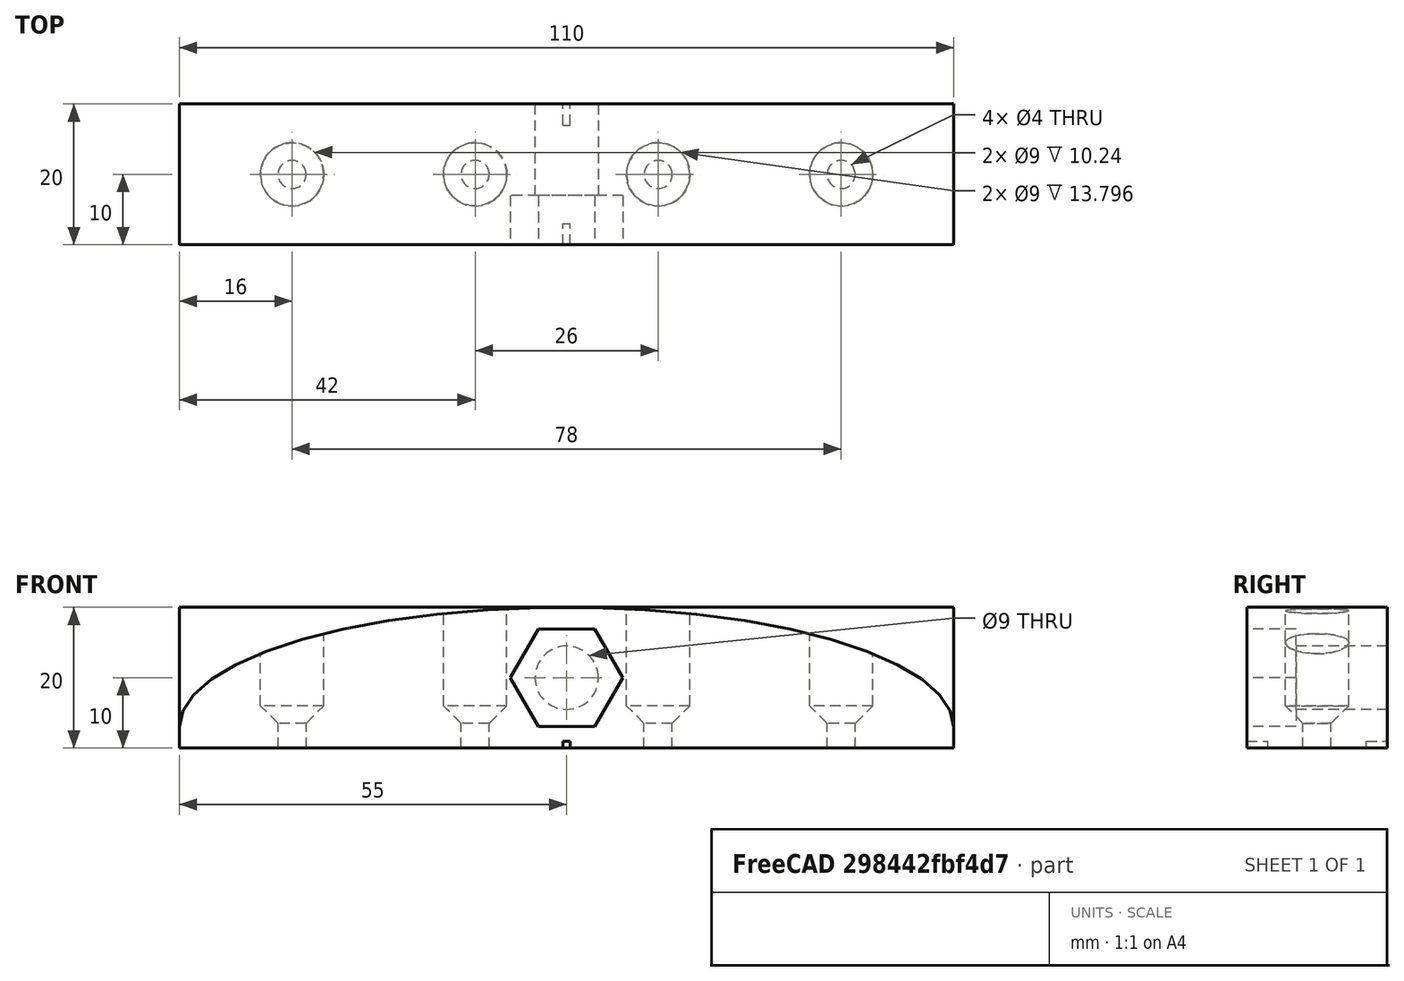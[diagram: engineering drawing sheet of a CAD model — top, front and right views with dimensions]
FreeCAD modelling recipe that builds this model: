
FCSTD DOCUMENT  (FreeCAD 0.18R4 (GitTag))
Label: Internal Support
License: All rights reserved
LicenseURL: http://en.wikipedia.org/wiki/All_rights_reserved
objects: Part::Box×5, Part::Cut×5, Part::Cylinder×4, Part::MultiFuse×4, Part::Extrusion×2, Part::Ellipse×1, Part::FeaturePython×1, Part::RegularPolygon×1, Part::Chamfer×1
note: 24 computed .brp shape members not serialized (recipe doc carries the construction recipe); baked Part::Feature solids carry a one-line shape summary decoded from their .brp

FEATURE [Part::Box] Box004  label="Signal003"
  AttacherType = Attacher::AttachEngine3D
  Height = 1
  Length = 1
  Placement = pos=(-0.5,7,0) rot=(0,0,1;0rad)
  Width = 3
FEATURE [Part::Cylinder] Cylinder005  label="Cylinder006"
  Angle = 360
  AttacherType = Attacher::AttachEngine3D
  Height = 20
  Placement = pos=(0,10,10) rot=(1,0,0;1.5708rad)
  Radius = 6.5
FEATURE [Part::Box] Box005  label="Signal004"
  AttacherType = Attacher::AttachEngine3D
  Height = 1
  Length = 1
  Placement = pos=(-0.5,-10,0) rot=(0,0,1;0rad)
  Width = 3
FEATURE [Part::Cylinder] Cylinder006  label="Hole001"
  Angle = 360
  AttacherType = Attacher::AttachEngine3D
  Height = 20
  Placement = pos=(0,10,10) rot=(1,0,0;1.5708rad)
  Radius = 4.5
FEATURE [Part::Ellipse] Ellipse
  Angle0 = 0
  Angle1 = 360
  AttacherType = Attacher::AttachEngine3D
  MajorRadius = 55
  MinorRadius = 17
  Placement = pos=(0,0,3) rot=(1,0,0;1.5708rad)
FEATURE [Part::Extrusion] Extrude002
  Base = -> Ellipse
  Dir = (0,1,0)
  DirMode = 2
  FaceMakerClass = Part::FaceMakerBullseye
  LengthFwd = 20
  LengthRev = 0
  Solid = true
  Symmetric = true
FEATURE [Part::Box] Box006  label="Cube001"
  AttacherType = Attacher::AttachEngine3D
  Height = 30
  Length = 110
  Placement = pos=(-55,-10,-27) rot=(0,0,1;0rad)
  Width = 20
FEATURE [Part::Cut] Cut008  label="Ellipsoid002"
  Base = -> Extrude002
  Refine = true
  Tool = -> Box006
FEATURE [Part::MultiFuse] Fusion
  Refine = true
  Shapes = -> [Cylinder005,Cut008]
FEATURE [Part::Cut] Cut009  label="Ellipsoid"
  Base = -> Fusion
  Refine = true
  Tool = -> Cylinder006
FEATURE [Part::Box] Box  label="Cube"
  AttacherType = Attacher::AttachEngine3D
  Height = 3
  Length = 110
  Placement = pos=(-55,-10,0) rot=(0,0,1;0rad)
  Width = 20
FEATURE [Part::MultiFuse] Fusion010  label="References001"
  Refine = true
  Shapes = -> [Box005,Box004]
FEATURE [Part::Cut] Cut007  label="Base"
  Base = -> Box
  Refine = true
  Tool = -> Fusion010
FEATURE [Part::MultiFuse] Fusion011  label="Support"
  Refine = true
  Shapes = -> [Cut007,Cut009]
FEATURE [Part::Box] Box001  label="Boundinbox"
  AttacherType = Attacher::AttachEngine3D
  Height = 20
  Length = 110
  Placement = pos=(-55,-10,0) rot=(0,0,1;0rad)
  Width = 20
FEATURE [Part::Cylinder] Cylinder004  label="Cylinder007"
  Angle = 360
  AttacherType = Attacher::AttachEngine3D
  Height = 20
  Placement = pos=(0,0,6) rot=(0,0,1;0rad)
  Radius = 4.5
FEATURE [Part::Cylinder] Cylinder007  label="Cylinder004"
  Angle = 360
  AttacherType = Attacher::AttachEngine3D
  Height = 25
  Radius = 2
FEATURE [Part::MultiFuse] Fusion008  label="screw hole 002"
  Refine = true
  Shapes = -> [Cylinder004,Cylinder007]
FEATURE [Part::FeaturePython] Array001  # Draft array (typed FeaturePython)
  Angle = 360
  ArrayType = 0
  Axis = (0,0,1)
  Base = -> Fusion008
  Center = (0,0,0)
  Fuse = false
  IntervalAxis = (0,0,0)
  IntervalX = (26,0,0)
  IntervalY = (0,0,0)
  IntervalZ = (0,0,0)
  NumberPolar = 1
  NumberX = 4
  NumberY = 1
  NumberZ = 1
  Placement = pos=(-39,0,0) rot=(0,0,1;0rad)
FEATURE [Part::RegularPolygon] RegularPolygon  label="Regular polygon"
  AttacherType = Attacher::AttachEngine3D
  Circumradius = 8
  Polygon = 6
FEATURE [Part::Extrusion] Extrude  label="Thread hole"
  Base = -> RegularPolygon
  Dir = (0,0,1)
  DirMode = 2
  FaceMakerClass = Part::FaceMakerBullseye
  LengthFwd = 7
  LengthRev = 0
  Placement = pos=(0,-3,10) rot=(1,0,0;1.5708rad)
  Solid = true
  Symmetric = false
FEATURE [Part::Cut] Cut  label="Support001"
  Base = -> Fusion011
  Refine = true
  Tool = -> Extrude
FEATURE [Part::Cut] Cut010  label="Internal Support"
  Base = -> Cut
  Refine = true
  Tool = -> Array001
FEATURE [Part::Chamfer] Chamfer
  Base = -> Cut010
  Edges = 4 edges r=2.49: [Edge78,Edge80,Edge82,Edge84]
